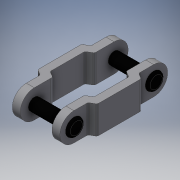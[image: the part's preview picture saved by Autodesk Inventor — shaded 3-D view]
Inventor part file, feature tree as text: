
AUTODESK INVENTOR PART (.ipt)
format: ipt  version: 2018.1 (Build 221151000, 151)  size: 237,056 bytes
history: native  units: in
note: dims shown in document units (in); Inventor stores cm internally (conversion verified against a paired STEP export)
features: fillet x4, hole x2, sketch x2, extrude x1, revolve x1, mirror x1
ambient origin geometry x8: Origin, YZ Plane, XZ Plane, XY Plane, X Axis, Y Axis, Z Axis, Center Point
bodies: Solid2 (feature_tree), Solid3 (feature_tree)
feature tree (11):
  extrude  "Extrusion1"  Depth=0.438in
  fillet  "Fillet1"  Radius=1.0in
  fillet  "Fillet2"  [1 undecoded]
  fillet  "Fillet3"  Radius=0.248in
  fillet  "Fillet4"  Radius=0.4961in
  hole  "Hole1"  [1 undecoded]
  hole  "Hole2"  [1 undecoded]
  revolve  "Revolution1"  [1 undecoded]
  mirror  "Mirror1"
  sketch  "Sketch1"  dims[d0=0.438in d1=0.0in d2=1.0in d3=1.0in]
  sketch  "Sketch2"  dims[d4=0.189in d5=0.75in d6=0.375in d7=0.25in d8=0.5635in d9=1.0in d10=0.8108in d11=1.0in d12=1.0in d13=0.189in d14=0.75in d15=0.375in d16=0.25in d17=0.5635in d18=1.0in d19=0.8108in d20=90.0deg d21=0.248in d22=0.4961in]
note: 4 required parameter values undecoded (feature->parameter linkage not recoverable at this tier; creation-order binding heuristic only, values carry confidence <= 0.55)
